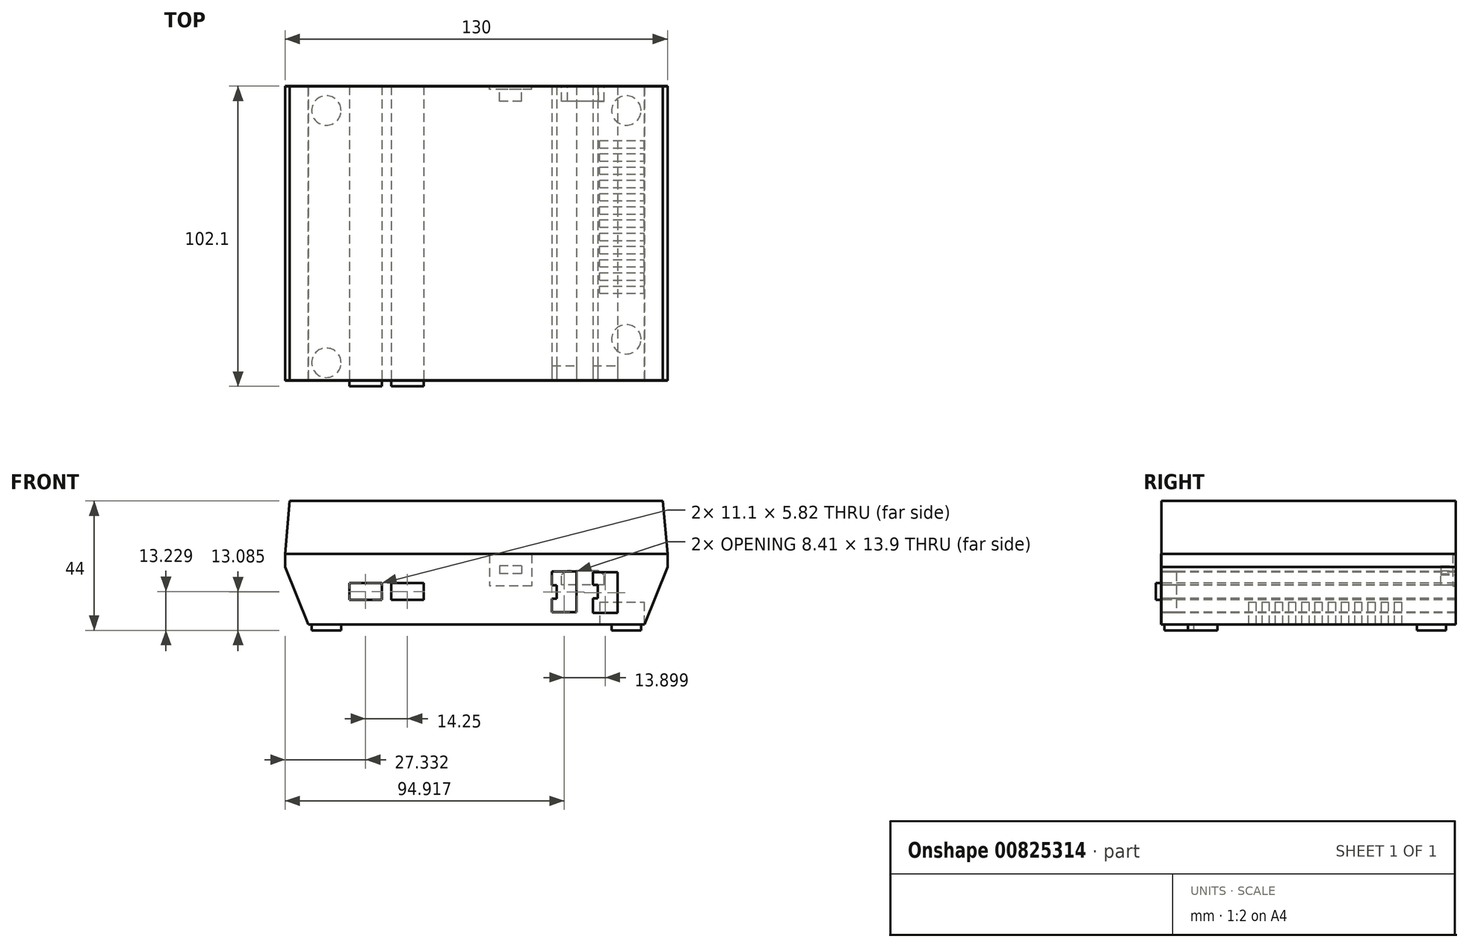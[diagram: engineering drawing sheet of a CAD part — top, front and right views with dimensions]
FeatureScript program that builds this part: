
annotation { "Feature Type Name" : "Feature", "Feature Type Description" : "" }
export const myFeature = defineFeature(function(context is Context, id is Id, definition is map)
    precondition{}
    {
        {
            var Q0;
            Q0=qCreatedBy(makeId("Top.planeOp"),FACE);
            var sketch = newSketch(context, id + "F0", { "sketchPlane" : qUnion([Q0])});
            skLineSegment(sketch, "E0.bottom", {"start": v(-113.03, 82.55) * mm, "end": v(113.03, 82.55) * mm});
            skLineSegment(sketch, "E0.top", {"start": v(-113.03, -82.55) * mm, "end": v(113.03, -82.55) * mm});
            skLineSegment(sketch, "E0.left", {"start": v(-113.03, 82.55) * mm, "end": v(-113.03, -82.55) * mm});
            skLineSegment(sketch, "E0.right", {"start": v(113.03, 82.55) * mm, "end": v(113.03, -82.55) * mm});
            skPoint(sketch, "E0.middle", {"position": v(0, 0) * mm});
            skSolve(sketch);
        }
        {
            var Q0;
            Q0=qCreatedBy(makeId("Front.planeOp"),FACE);
            var sketch = newSketch(context, id + "F1", { "sketchPlane" : qUnion([Q0])});
            skLineSegment(sketch, "E1.0", {"start": v(-57.12, 0) * mm, "end": v(57.12, 0) * mm});
            skLineSegment(sketch, "E2", {"start": v(-65, 19.5) * mm, "end": v(-65, 24) * mm});
            skLineSegment(sketch, "E3", {"start": v(-63.43, 42) * mm, "end": v(63.43, 42) * mm});
            skLineSegment(sketch, "E4", {"start": v(65, 24) * mm, "end": v(65, 19.5) * mm});
            skLineSegment(sketch, "E5", {"start": v(-57.12, 0) * mm, "end": v(-65, 19.5) * mm});
            skLineSegment(sketch, "E6", {"start": v(-65, 24) * mm, "end": v(-63.43, 42) * mm});
            skLineSegment(sketch, "E7", {"start": v(63.43, 42) * mm, "end": v(65, 24) * mm});
            skLineSegment(sketch, "E8", {"start": v(65, 19.5) * mm, "end": v(57.12, 0) * mm});
            skLineSegment(sketch, "E9", {"start": v(57.12, 0) * mm, "end": v(-57.12, 0) * mm});
            skPoint(sketch, "E10", {"position": v(0, 42) * mm});
            skLineSegment(sketch, "E11", {"start": v(0, 42) * mm, "end": v(0, 0) * mm, "construction": true});
            skPoint(sketch, "E12", {"position": v(0, 21) * mm});
            skSolve(sketch);
        }
        {
            var Q0;
            Q0=makeQuery(id+"F1.imprint","IMPRINT",FACE,{"disambiguationData":[TD([[makeQuery(id+"F1.imprint","IMPRINT",EDGE,{"derivedFrom":sQuery(id+"F1.wireOp",EDGE,"E5")}),-1.0]])]});
            extrude(context, id + "F2", {"entities" : qUnion([Q0]), "endBound" : BoundingType.SYMMETRIC, "depth" : 100 * mm, "offsetDistance" : 25.4 * mm});
        }
        {
            var Q0;
            Q0=makeQuery(id+"F2.opExtrude","CAP_FACE",FACE,{"disambiguationData":[OSD([sQuery(id+"F1.wireOp",EDGE,"E5"),sQuery(id+"F1.wireOp",EDGE,"E2"),sQuery(id+"F1.wireOp",EDGE,"E6"),sQuery(id+"F1.wireOp",EDGE,"E3"),sQuery(id+"F1.wireOp",EDGE,"E7"),sQuery(id+"F1.wireOp",EDGE,"E4"),sQuery(id+"F1.wireOp",EDGE,"E8"),sQuery(id+"F1.wireOp",EDGE,"E9")])],"isStart":false});
            var sketch = newSketch(context, id + "F3", { "sketchPlane" : qUnion([Q0])});
            skLineSegment(sketch, "E13.bottom", {"start": v(-43.22, 8.32) * mm, "end": v(-32.12, 8.32) * mm});
            skLineSegment(sketch, "E13.top", {"start": v(-43.22, 14.14) * mm, "end": v(-32.12, 14.14) * mm});
            skLineSegment(sketch, "E13.left", {"start": v(-43.22, 8.32) * mm, "end": v(-43.22, 14.14) * mm});
            skLineSegment(sketch, "E13.right", {"start": v(-32.12, 8.32) * mm, "end": v(-32.12, 14.14) * mm});
            skLineSegment(sketch, "E14.bottom", {"start": v(-28.96, 14.14) * mm, "end": v(-17.87, 14.14) * mm});
            skLineSegment(sketch, "E14.top", {"start": v(-28.96, 8.32) * mm, "end": v(-17.87, 8.32) * mm});
            skLineSegment(sketch, "E14.left", {"start": v(-28.96, 14.14) * mm, "end": v(-28.96, 8.32) * mm});
            skLineSegment(sketch, "E14.right", {"start": v(-17.87, 14.14) * mm, "end": v(-17.87, 8.32) * mm});
            skLineSegment(sketch, "E15.bottom", {"start": v(25.71, 18.03) * mm, "end": v(34.12, 18.03) * mm});
            skLineSegment(sketch, "E15.top", {"start": v(25.71, 4.14) * mm, "end": v(34.12, 4.14) * mm});
            skLineSegment(sketch, "E15.left", {"start": v(25.71, 18.03) * mm, "end": v(25.71, 13.32) * mm});
            skLineSegment(sketch, "E15.right", {"start": v(34.12, 18.03) * mm, "end": v(34.12, 4.14) * mm});
            skLineSegment(sketch, "E16.bottom", {"start": v(25.71, 13.32) * mm, "end": v(27.34, 13.32) * mm});
            skLineSegment(sketch, "E16.top", {"start": v(25.71, 8.77) * mm, "end": v(27.34, 8.77) * mm});
            skLineSegment(sketch, "E16.right", {"start": v(27.34, 13.32) * mm, "end": v(27.34, 8.77) * mm});
            skLineSegment(sketch, "E17.bottom", {"start": v(39.61, 17.78) * mm, "end": v(48.02, 17.78) * mm});
            skLineSegment(sketch, "E17.top", {"start": v(39.61, 3.88) * mm, "end": v(48.02, 3.88) * mm});
            skLineSegment(sketch, "E17.left", {"start": v(39.61, 17.78) * mm, "end": v(39.61, 13.49) * mm});
            skLineSegment(sketch, "E17.right", {"start": v(48.02, 17.78) * mm, "end": v(48.02, 3.88) * mm});
            skLineSegment(sketch, "E18.bottom", {"start": v(39.61, 13.49) * mm, "end": v(41.24, 13.49) * mm});
            skLineSegment(sketch, "E18.top", {"start": v(39.61, 8.94) * mm, "end": v(41.24, 8.94) * mm});
            skLineSegment(sketch, "E18.right", {"start": v(41.24, 13.49) * mm, "end": v(41.24, 8.94) * mm});
            skLineSegment(sketch, "E19.trimOffspring", {"start": v(25.71, 8.77) * mm, "end": v(25.71, 4.14) * mm});
            skLineSegment(sketch, "E20.trimOffspring", {"start": v(39.61, 8.94) * mm, "end": v(39.61, 3.88) * mm});
            skSolve(sketch);
        }
        {
            var Q0;
            Q0=makeQuery(id+"F3.imprint","IMPRINT",FACE,{"disambiguationData":[TD([[makeQuery(id+"F3.imprint","IMPRINT",EDGE,{"derivedFrom":sQuery(id+"F3.wireOp",EDGE,"E13.bottom")}),1.0]])]});
            var Q1;
            Q1=makeQuery(id+"F3.imprint","IMPRINT",FACE,{"disambiguationData":[TD([[makeQuery(id+"F3.imprint","IMPRINT",EDGE,{"derivedFrom":sQuery(id+"F3.wireOp",EDGE,"E14.bottom")}),-1.0]])]});
            extrude(context, id + "F4", {"entities" : qUnion([Q0, Q1]), "operationType" : NewBodyOperationType.ADD, "depth" : 2 * mm, "offsetDistance" : 25.4 * mm});
        }
        {
            var Q0;
            Q0=makeQuery(id+"F3.imprint","IMPRINT",FACE,{"disambiguationData":[TD([[makeQuery(id+"F3.imprint","IMPRINT",EDGE,{"derivedFrom":sQuery(id+"F3.wireOp",EDGE,"E15.bottom")}),-1.0]])]});
            var Q1;
            Q1=makeQuery(id+"F3.imprint","IMPRINT",FACE,{"disambiguationData":[TD([[makeQuery(id+"F3.imprint","IMPRINT",EDGE,{"derivedFrom":sQuery(id+"F3.wireOp",EDGE,"E17.bottom")}),-1.0]])]});
            extrude(context, id + "F5", {"entities" : qUnion([Q0, Q1]), "operationType" : NewBodyOperationType.REMOVE, "oppositeDirection" : true, "depth" : 5 * mm, "offsetDistance" : 25.4 * mm});
        }
        {
            var Q0;
            Q0=makeQuery(id+"F2.opExtrude","CAP_FACE",FACE,{"disambiguationData":[OSD([sQuery(id+"F1.wireOp",EDGE,"E5"),sQuery(id+"F1.wireOp",EDGE,"E2"),sQuery(id+"F1.wireOp",EDGE,"E6"),sQuery(id+"F1.wireOp",EDGE,"E3"),sQuery(id+"F1.wireOp",EDGE,"E7"),sQuery(id+"F1.wireOp",EDGE,"E4"),sQuery(id+"F1.wireOp",EDGE,"E8"),sQuery(id+"F1.wireOp",EDGE,"E9")])],"isStart":true});
            var sketch = newSketch(context, id + "F6", { "sketchPlane" : qUnion([Q0])});
            skPoint(sketch, "E21", {"position": v(0, 42.6) * mm});
            skLineSegment(sketch, "E22.bottom", {"start": v(-43.5, 13.5) * mm, "end": v(-29, 13.5) * mm});
            skLineSegment(sketch, "E22.top", {"start": v(-41.5, 18.3) * mm, "end": v(-31, 18.3) * mm});
            skLineSegment(sketch, "E22.left", {"start": v(-43.5, 13.5) * mm, "end": v(-43.5, 16.9) * mm});
            skLineSegment(sketch, "E22.right", {"start": v(-29, 13.5) * mm, "end": v(-29, 16.9) * mm});
            skLineSegment(sketch, "E23", {"start": v(-41.5, 18.3) * mm, "end": v(-43.5, 16.9) * mm});
            skLineSegment(sketch, "E24", {"start": v(-31, 18.3) * mm, "end": v(-29, 16.9) * mm});
            skPoint(sketch, "E25", {"position": v(-36.25, 18.3) * mm});
            skPoint(sketch, "E26", {"position": v(-36.25, 13.5) * mm});
            skLineSegment(sketch, "E27.bottom", {"start": v(-15.4, 19.9) * mm, "end": v(-7.9, 19.9) * mm});
            skLineSegment(sketch, "E27.top", {"start": v(-15.4, 17.2) * mm, "end": v(-7.9, 17.2) * mm});
            skLineSegment(sketch, "E27.left", {"start": v(-15.4, 19.9) * mm, "end": v(-15.4, 17.2) * mm});
            skLineSegment(sketch, "E27.right", {"start": v(-7.9, 19.9) * mm, "end": v(-7.9, 17.2) * mm});
            skLineSegment(sketch, "E28.bottom", {"start": v(-18.8, 23.8) * mm, "end": v(-4.5, 23.8) * mm});
            skLineSegment(sketch, "E28.top", {"start": v(-18.8, 13.1) * mm, "end": v(-4.5, 13.1) * mm});
            skLineSegment(sketch, "E28.left", {"start": v(-18.8, 23.8) * mm, "end": v(-18.8, 13.1) * mm});
            skLineSegment(sketch, "E28.right", {"start": v(-4.5, 23.8) * mm, "end": v(-4.5, 13.1) * mm});
            skSolve(sketch);
        }
        {
            var Q0;
            Q0=makeQuery(id+"F6.imprint","IMPRINT",FACE,{"disambiguationData":[TD([[makeQuery(id+"F6.imprint","IMPRINT",EDGE,{"derivedFrom":sQuery(id+"F6.wireOp",EDGE,"E22.bottom")}),1.0]])]});
            var Q1;
            Q1=makeQuery(id+"F6.imprint","IMPRINT",FACE,{"disambiguationData":[TD([[makeQuery(id+"F6.imprint","IMPRINT",EDGE,{"derivedFrom":sQuery(id+"F6.wireOp",EDGE,"E27.bottom")}),-1.0]])]});
            extrude(context, id + "F7", {"entities" : qUnion([Q0, Q1]), "operationType" : NewBodyOperationType.REMOVE, "oppositeDirection" : true, "depth" : 5.08 * mm, "offsetDistance" : 25.4 * mm});
        }
        {
            var Q0;
            Q0=makeQuery(id+"F6.imprint","IMPRINT",FACE,{"disambiguationData":[TD([[makeQuery(id+"F6.imprint","IMPRINT",EDGE,{"derivedFrom":sQuery(id+"F6.wireOp",EDGE,"E27.bottom")}),1.0]])]});
            extrude(context, id + "F8", {"entities" : qUnion([Q0]), "operationType" : NewBodyOperationType.REMOVE, "oppositeDirection" : true, "depth" : 1 * mm, "offsetDistance" : 25.4 * mm});
        }
        {
            var Q0;
            Q0=makeQuery(id+"F0.imprint","IMPRINT",FACE,{"disambiguationData":[TD([[makeQuery(id+"F0.imprint","IMPRINT",EDGE,{"derivedFrom":sQuery(id+"F0.wireOp",EDGE,"E0.bottom")}),-1.0]])]});
            var sketch = newSketch(context, id + "F9", { "sketchPlane" : qUnion([Q0])});
            skPoint(sketch, "E29", {"position": v(0, -50) * mm});
            skLineSegment(sketch, "E30.bottom", {"start": v(41.9, -20.4) * mm, "end": v(57, -20.4) * mm});
            skLineSegment(sketch, "E30.top", {"start": v(41.9, -17.9) * mm, "end": v(57, -17.9) * mm});
            skLineSegment(sketch, "E30.left", {"start": v(41.9, -20.4) * mm, "end": v(41.9, -17.9) * mm});
            skLineSegment(sketch, "E30.right", {"start": v(57, -20.4) * mm, "end": v(57, -17.9) * mm});
            skLineSegment(sketch, "E31.0.1.0", {"start": v(41.9, -13.4) * mm, "end": v(57, -13.4) * mm});
            skLineSegment(sketch, "E31.0.1.1", {"start": v(41.9, -15.9) * mm, "end": v(57, -15.9) * mm});
            skLineSegment(sketch, "E31.0.1.2", {"start": v(41.9, -15.9) * mm, "end": v(41.9, -13.4) * mm});
            skLineSegment(sketch, "E31.0.1.3", {"start": v(57, -15.9) * mm, "end": v(57, -13.4) * mm});
            skLineSegment(sketch, "E31.0.2.0", {"start": v(41.9, -8.9) * mm, "end": v(57, -8.9) * mm});
            skLineSegment(sketch, "E31.0.2.1", {"start": v(41.9, -11.4) * mm, "end": v(57, -11.4) * mm});
            skLineSegment(sketch, "E31.0.2.2", {"start": v(41.9, -11.4) * mm, "end": v(41.9, -8.9) * mm});
            skLineSegment(sketch, "E31.0.2.3", {"start": v(57, -11.4) * mm, "end": v(57, -8.9) * mm});
            skLineSegment(sketch, "E31.0.3.0", {"start": v(41.9, -4.4) * mm, "end": v(57, -4.4) * mm});
            skLineSegment(sketch, "E31.0.3.1", {"start": v(41.9, -6.9) * mm, "end": v(57, -6.9) * mm});
            skLineSegment(sketch, "E31.0.3.2", {"start": v(41.9, -6.9) * mm, "end": v(41.9, -4.4) * mm});
            skLineSegment(sketch, "E31.0.3.3", {"start": v(57, -6.9) * mm, "end": v(57, -4.4) * mm});
            skLineSegment(sketch, "E31.0.4.0", {"start": v(41.9, 0.1) * mm, "end": v(57, 0.1) * mm});
            skLineSegment(sketch, "E31.0.4.1", {"start": v(41.9, -2.4) * mm, "end": v(57, -2.4) * mm});
            skLineSegment(sketch, "E31.0.4.2", {"start": v(41.9, -2.4) * mm, "end": v(41.9, 0.1) * mm});
            skLineSegment(sketch, "E31.0.4.3", {"start": v(57, -2.4) * mm, "end": v(57, 0.1) * mm});
            skLineSegment(sketch, "E31.0.5.0", {"start": v(41.9, 4.6) * mm, "end": v(57, 4.6) * mm});
            skLineSegment(sketch, "E31.0.5.1", {"start": v(41.9, 2.1) * mm, "end": v(57, 2.1) * mm});
            skLineSegment(sketch, "E31.0.5.2", {"start": v(41.9, 2.1) * mm, "end": v(41.9, 4.6) * mm});
            skLineSegment(sketch, "E31.0.5.3", {"start": v(57, 2.1) * mm, "end": v(57, 4.6) * mm});
            skLineSegment(sketch, "E31.0.6.0", {"start": v(41.9, 9.1) * mm, "end": v(57, 9.1) * mm});
            skLineSegment(sketch, "E31.0.6.1", {"start": v(41.9, 6.6) * mm, "end": v(57, 6.6) * mm});
            skLineSegment(sketch, "E31.0.6.2", {"start": v(41.9, 6.6) * mm, "end": v(41.9, 9.1) * mm});
            skLineSegment(sketch, "E31.0.6.3", {"start": v(57, 6.6) * mm, "end": v(57, 9.1) * mm});
            skLineSegment(sketch, "E31.0.7.0", {"start": v(41.9, 13.6) * mm, "end": v(57, 13.6) * mm});
            skLineSegment(sketch, "E31.0.7.1", {"start": v(41.9, 11.1) * mm, "end": v(57, 11.1) * mm});
            skLineSegment(sketch, "E31.0.7.2", {"start": v(41.9, 11.1) * mm, "end": v(41.9, 13.6) * mm});
            skLineSegment(sketch, "E31.0.7.3", {"start": v(57, 11.1) * mm, "end": v(57, 13.6) * mm});
            skLineSegment(sketch, "E31.0.8.0", {"start": v(41.9, 18.1) * mm, "end": v(57, 18.1) * mm});
            skLineSegment(sketch, "E31.0.8.1", {"start": v(41.9, 15.6) * mm, "end": v(57, 15.6) * mm});
            skLineSegment(sketch, "E31.0.8.2", {"start": v(41.9, 15.6) * mm, "end": v(41.9, 18.1) * mm});
            skLineSegment(sketch, "E31.0.8.3", {"start": v(57, 15.6) * mm, "end": v(57, 18.1) * mm});
            skLineSegment(sketch, "E31.0.9.0", {"start": v(41.9, 22.6) * mm, "end": v(57, 22.6) * mm});
            skLineSegment(sketch, "E31.0.9.1", {"start": v(41.9, 20.1) * mm, "end": v(57, 20.1) * mm});
            skLineSegment(sketch, "E31.0.9.2", {"start": v(41.9, 20.1) * mm, "end": v(41.9, 22.6) * mm});
            skLineSegment(sketch, "E31.0.9.3", {"start": v(57, 20.1) * mm, "end": v(57, 22.6) * mm});
            skLineSegment(sketch, "E31.0.10.0", {"start": v(41.9, 27.1) * mm, "end": v(57, 27.1) * mm});
            skLineSegment(sketch, "E31.0.10.1", {"start": v(41.9, 24.6) * mm, "end": v(57, 24.6) * mm});
            skLineSegment(sketch, "E31.0.10.2", {"start": v(41.9, 24.6) * mm, "end": v(41.9, 27.1) * mm});
            skLineSegment(sketch, "E31.0.10.3", {"start": v(57, 24.6) * mm, "end": v(57, 27.1) * mm});
            skLineSegment(sketch, "E31.0.11.0", {"start": v(41.9, 31.6) * mm, "end": v(57, 31.6) * mm});
            skLineSegment(sketch, "E31.0.11.1", {"start": v(41.9, 29.1) * mm, "end": v(57, 29.1) * mm});
            skLineSegment(sketch, "E31.0.11.2", {"start": v(41.9, 29.1) * mm, "end": v(41.9, 31.6) * mm});
            skLineSegment(sketch, "E31.0.11.3", {"start": v(57, 29.1) * mm, "end": v(57, 31.6) * mm});
            skLineSegment(sketch, "E31.direction1", {"start": v(41.9, -20.4) * mm, "end": v(66.9, -20.4) * mm, "construction": true});
            skLineSegment(sketch, "E31.direction2", {"start": v(41.9, -20.4) * mm, "end": v(41.9, -15.9) * mm, "construction": true});
            skCircle(sketch, "E32", {"center": v(51, -36) * mm, "radius": 5 * mm});
            skCircle(sketch, "E33", {"center": v(-51, -44) * mm, "radius": 5 * mm});
            skCircle(sketch, "E34", {"center": v(-51, 41.8) * mm, "radius": 5 * mm});
            skCircle(sketch, "E35", {"center": v(51, 41.8) * mm, "radius": 5 * mm});
            skSolve(sketch);
        }
        {
            var Q0;
            Q0=makeQuery(id+"F9.imprint","IMPRINT",FACE,{"disambiguationData":[TD([[makeQuery(id+"F9.imprint","IMPRINT",EDGE,{"derivedFrom":sQuery(id+"F9.wireOp",EDGE,"E30.bottom")}),1.0]])]});
            var Q1;
            Q1=makeQuery(id+"F9.imprint","IMPRINT",FACE,{"disambiguationData":[TD([[makeQuery(id+"F9.imprint","IMPRINT",EDGE,{"derivedFrom":sQuery(id+"F9.wireOp",EDGE,"E31.0.1.0")}),-1.0]])]});
            var Q2;
            Q2=makeQuery(id+"F9.imprint","IMPRINT",FACE,{"disambiguationData":[TD([[makeQuery(id+"F9.imprint","IMPRINT",EDGE,{"derivedFrom":sQuery(id+"F9.wireOp",EDGE,"E31.0.2.0")}),-1.0]])]});
            var Q3;
            Q3=makeQuery(id+"F9.imprint","IMPRINT",FACE,{"disambiguationData":[TD([[makeQuery(id+"F9.imprint","IMPRINT",EDGE,{"derivedFrom":sQuery(id+"F9.wireOp",EDGE,"E31.0.3.0")}),-1.0]])]});
            var Q4;
            Q4=makeQuery(id+"F9.imprint","IMPRINT",FACE,{"disambiguationData":[TD([[makeQuery(id+"F9.imprint","IMPRINT",EDGE,{"derivedFrom":sQuery(id+"F9.wireOp",EDGE,"E31.0.4.0")}),-1.0]])]});
            var Q5;
            Q5=makeQuery(id+"F9.imprint","IMPRINT",FACE,{"disambiguationData":[TD([[makeQuery(id+"F9.imprint","IMPRINT",EDGE,{"derivedFrom":sQuery(id+"F9.wireOp",EDGE,"E31.0.5.0")}),-1.0]])]});
            var Q6;
            Q6=makeQuery(id+"F9.imprint","IMPRINT",FACE,{"disambiguationData":[TD([[makeQuery(id+"F9.imprint","IMPRINT",EDGE,{"derivedFrom":sQuery(id+"F9.wireOp",EDGE,"E31.0.6.0")}),-1.0]])]});
            var Q7;
            Q7=makeQuery(id+"F9.imprint","IMPRINT",FACE,{"disambiguationData":[TD([[makeQuery(id+"F9.imprint","IMPRINT",EDGE,{"derivedFrom":sQuery(id+"F9.wireOp",EDGE,"E31.0.7.0")}),-1.0]])]});
            var Q8;
            Q8=makeQuery(id+"F9.imprint","IMPRINT",FACE,{"disambiguationData":[TD([[makeQuery(id+"F9.imprint","IMPRINT",EDGE,{"derivedFrom":sQuery(id+"F9.wireOp",EDGE,"E31.0.8.0")}),-1.0]])]});
            var Q9;
            Q9=makeQuery(id+"F9.imprint","IMPRINT",FACE,{"disambiguationData":[TD([[makeQuery(id+"F9.imprint","IMPRINT",EDGE,{"derivedFrom":sQuery(id+"F9.wireOp",EDGE,"E31.0.9.0")}),-1.0]])]});
            var Q10;
            Q10=makeQuery(id+"F9.imprint","IMPRINT",FACE,{"disambiguationData":[TD([[makeQuery(id+"F9.imprint","IMPRINT",EDGE,{"derivedFrom":sQuery(id+"F9.wireOp",EDGE,"E31.0.10.0")}),-1.0]])]});
            var Q11;
            Q11=makeQuery(id+"F9.imprint","IMPRINT",FACE,{"disambiguationData":[TD([[makeQuery(id+"F9.imprint","IMPRINT",EDGE,{"derivedFrom":sQuery(id+"F9.wireOp",EDGE,"E31.0.11.0")}),-1.0]])]});
            extrude(context, id + "F10", {"entities" : qUnion([Q0, Q1, Q2, Q3, Q4, Q5, Q6, Q7, Q8, Q9, Q10, Q11]), "operationType" : NewBodyOperationType.REMOVE, "depth" : 7.62 * mm, "offsetDistance" : 25.4 * mm});
        }
        {
            var Q0;
            Q0=makeQuery(id+"F9.imprint","IMPRINT",FACE,{"disambiguationData":[TD([[makeQuery(id+"F9.imprint","IMPRINT",EDGE,{"derivedFrom":sQuery(id+"F9.wireOp",EDGE,"E33")}),1.0]])]});
            var Q1;
            Q1=makeQuery(id+"F9.imprint","IMPRINT",FACE,{"disambiguationData":[TD([[makeQuery(id+"F9.imprint","IMPRINT",EDGE,{"derivedFrom":sQuery(id+"F9.wireOp",EDGE,"E32")}),1.0]])]});
            var Q2;
            Q2=makeQuery(id+"F9.imprint","IMPRINT",FACE,{"disambiguationData":[TD([[makeQuery(id+"F9.imprint","IMPRINT",EDGE,{"derivedFrom":sQuery(id+"F9.wireOp",EDGE,"E35")}),1.0]])]});
            var Q3;
            Q3=makeQuery(id+"F9.imprint","IMPRINT",FACE,{"disambiguationData":[TD([[makeQuery(id+"F9.imprint","IMPRINT",EDGE,{"derivedFrom":sQuery(id+"F9.wireOp",EDGE,"E34")}),1.0]])]});
            extrude(context, id + "F11", {"entities" : qUnion([Q0, Q1, Q2, Q3]), "operationType" : NewBodyOperationType.ADD, "oppositeDirection" : true, "depth" : 2 * mm, "offsetDistance" : 25.4 * mm});
        }
        {
            var Q0;
            Q0=makeQuery(id+"F2.opExtrude","CAP_FACE",FACE,{"disambiguationData":[OSD([sQuery(id+"F1.wireOp",EDGE,"E5"),sQuery(id+"F1.wireOp",EDGE,"E2"),sQuery(id+"F1.wireOp",EDGE,"E6"),sQuery(id+"F1.wireOp",EDGE,"E3"),sQuery(id+"F1.wireOp",EDGE,"E7"),sQuery(id+"F1.wireOp",EDGE,"E4"),sQuery(id+"F1.wireOp",EDGE,"E8"),sQuery(id+"F1.wireOp",EDGE,"E9")])],"isStart":false});
            var sketch = newSketch(context, id + "F12", { "sketchPlane" : qUnion([Q0])});
            skLineSegment(sketch, "E36", {"start": v(-65.1, 24) * mm, "end": v(65.1, 24) * mm});
            skLineSegment(sketch, "E37.0", {"start": v(-65.1, 19.48) * mm, "end": v(-65.1, 24) * mm});
            skLineSegment(sketch, "E37.1", {"start": v(65.1, 24) * mm, "end": v(65.1, 19.48) * mm});
            skLineSegment(sketch, "E37.2", {"start": v(65.1, 19.48) * mm, "end": v(57.19, -0.1) * mm});
            skLineSegment(sketch, "E37.3", {"start": v(57.19, -0.1) * mm, "end": v(-57.19, -0.1) * mm});
            skLineSegment(sketch, "E37.4", {"start": v(-57.19, -0.1) * mm, "end": v(-65.1, 19.48) * mm});
            skPoint(sketch, "E38.0.start.orphan", {"position": v(57.12, 0) * mm});
            skPoint(sketch, "E39.0.start.orphan", {"position": v(-57.12, 0) * mm});
            skPoint(sketch, "E40.0.start.orphan", {"position": v(-65, 19.5) * mm});
            skSolve(sketch);
        }
        {
            var Q0;
            Q0=makeQuery(id+"F12.imprint","IMPRINT",FACE,{"disambiguationData":[TD([[makeQuery(id+"F12.imprint","IMPRINT",EDGE,{"derivedFrom":makeQuery(id+"F2.opExtrude","CAP_EDGE",EDGE,{"disambiguationData":[OSD([sQuery(id+"F1.wireOp",EDGE,"E5")])],"isStart":false})}),-1.0]])]});
            extrude(context, id + "F13", {"entities" : qUnion([Q0]), "oppositeDirection" : true, "depth" : 100.1 * mm, "offsetDistance" : 25 * mm, "hasSecondDirection" : true, "secondDirectionOppositeDirection" : false, "secondDirectionDepth" : .1 * mm});
        }
    });
